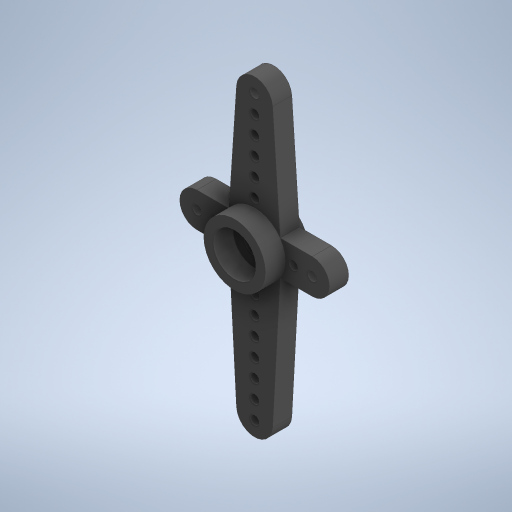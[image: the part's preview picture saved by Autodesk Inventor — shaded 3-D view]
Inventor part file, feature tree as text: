
AUTODESK INVENTOR PART (.ipt)
format: ipt  version: 2023 (Build 270158000, 158)  size: 414,720 bytes
history: native  units: mm
features: extrude x8, sketch x7, other x1
ambient origin geometry x8: Origin, YZ Plane, XZ Plane, XY Plane, X Axis, Y Axis, Z Axis, Center Point
bodies: Body1 (feature_tree)
feature tree (16):
  other  "솔리드1"
  sketch  "스케치1"
  extrude  "돌출1"  Depth=5.0mm
  extrude  "돌출2"  Depth=1.9mm
  extrude  "돌출3"  Depth=16.5mm
  extrude  "돌출4"  Depth=29.0mm
  extrude  "돌출5"  Depth=1.0mm
  sketch  "스케치4"
  extrude  "돌출6"  Depth=1.0mm
  extrude  "돌출7"  Depth=1.0mm
  extrude  "돌출8"  Depth=1.0mm
  sketch  "스케치2"
  sketch  "스케치3"
  sketch  "스케치5"
  sketch  "스케치6"
  sketch  "스케치7"
